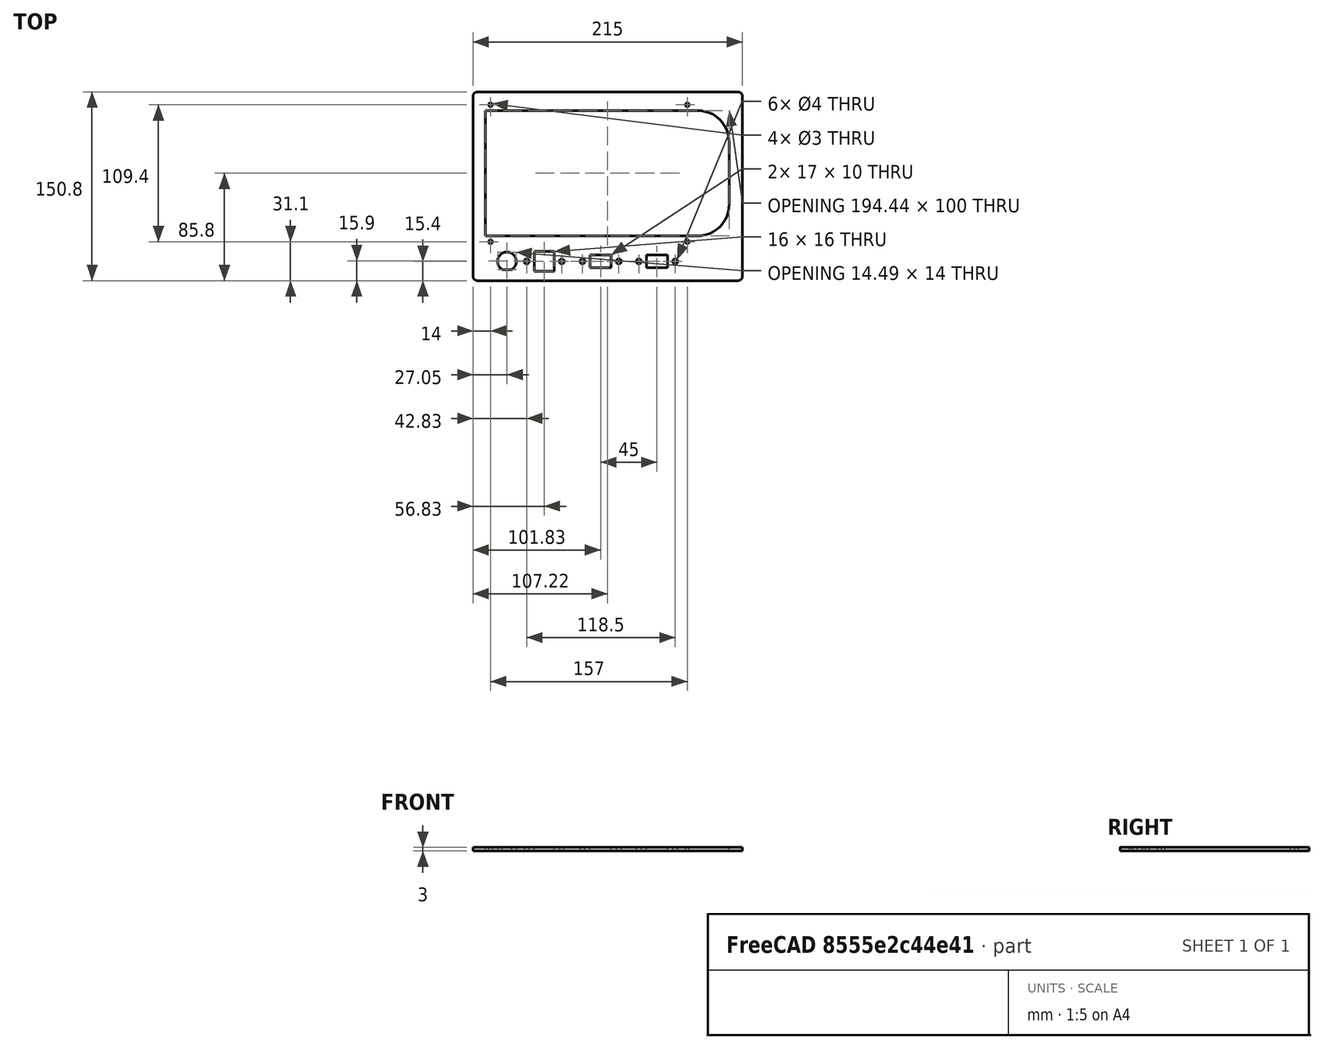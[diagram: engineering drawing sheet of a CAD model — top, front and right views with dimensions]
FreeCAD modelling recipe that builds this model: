
FCSTD DOCUMENT  (FreeCAD 0.20R29603 (Git))
Label: small
License: All rights reserved
LicenseURL: http://en.wikipedia.org/wiki/All_rights_reserved
objects: Sketcher::SketchObject×1, Part::Extrusion×1
note: 2 computed .brp shape members not serialized (recipe doc carries the construction recipe); baked Part::Feature solids carry a one-line shape summary decoded from their .brp

FEATURE [Sketcher::SketchObject] Sketch
  FullyConstrained = true
  sketch-geometry (74):
    g0: LineSegment StartX=-104 StartY=-75.4 StartZ=0 EndX=104 EndY=-75.4 EndZ=0
    g1: LineSegment StartX=107.5 StartY=-71.9 StartZ=0 EndX=107.5 EndY=71.9 EndZ=0
    g2: LineSegment StartX=104 StartY=75.4 StartZ=0 EndX=-104 EndY=75.4 EndZ=0
    g3: LineSegment StartX=-107.5 StartY=71.9 StartZ=0 EndX=-107.5 EndY=-71.9 EndZ=0
    g4: ArcOfCircle CenterX=-104 CenterY=71.9 CenterZ=0 NormalX=0 NormalY=0 NormalZ=1 AngleXU=0 Radius=3.5 StartAngle=1.5708 EndAngle=3.14159
    g5: ArcOfCircle CenterX=104 CenterY=71.9 CenterZ=0 NormalX=0 NormalY=0 NormalZ=1 AngleXU=0 Radius=3.5 StartAngle=-9e-16 EndAngle=1.5708
    g6: ArcOfCircle CenterX=104 CenterY=-71.9 CenterZ=0 NormalX=0 NormalY=0 NormalZ=1 AngleXU=0 Radius=3.5 StartAngle=4.71239 EndAngle=6.28319
    g7: ArcOfCircle CenterX=-104 CenterY=-71.9 CenterZ=0 NormalX=0 NormalY=0 NormalZ=1 AngleXU=0 Radius=3.5 StartAngle=3.14159 EndAngle=4.71239
    g8: LineSegment StartX=-97.5 StartY=-39.6 StartZ=0 EndX=67.5 EndY=-39.6 EndZ=0
    g9: LineSegment StartX=67.5 StartY=-39.6 StartZ=0 EndX=67.5 EndY=60.4 EndZ=0
    g10: LineSegment StartX=67.5 StartY=60.4 StartZ=0 EndX=-97.5 EndY=60.4 EndZ=0
    g11: LineSegment StartX=-97.5 StartY=60.4 StartZ=0 EndX=-97.5 EndY=-39.6 EndZ=0
    g12: Circle CenterX=-93.5 CenterY=65.1 CenterZ=0 NormalX=0 NormalY=0 NormalZ=1 AngleXU=0 Radius=1.5
    g13: Circle CenterX=63.5 CenterY=65.1 CenterZ=0 NormalX=0 NormalY=0 NormalZ=1 AngleXU=0 Radius=1.5
    g14: Circle CenterX=-93.5 CenterY=-44.3 CenterZ=0 NormalX=0 NormalY=0 NormalZ=1 AngleXU=0 Radius=1.5
    g15: Circle CenterX=63.5 CenterY=-44.3 CenterZ=0 NormalX=0 NormalY=0 NormalZ=1 AngleXU=0 Radius=1.5
    g16: LineSegment StartX=-97.5 StartY=60.4 StartZ=0 EndX=67.5 EndY=-39.6 EndZ=0
    g17: LineSegment StartX=-97.5 StartY=-39.6 StartZ=0 EndX=67.5 EndY=60.4 EndZ=0
    g18: GeomPoint X=-15 Y=10.4 Z=0
    g19: GeomPoint X=-15 Y=10.4 Z=0
    g20: LineSegment StartX=-15 StartY=65.1 StartZ=0 EndX=-15 EndY=10.4 EndZ=0
    g21: LineSegment StartX=-15 StartY=10.4 StartZ=0 EndX=-15 EndY=-44.3 EndZ=0
    g22: LineSegment StartX=-93.5 StartY=65.1 StartZ=0 EndX=63.5 EndY=65.1 EndZ=0
    g23: LineSegment StartX=-93.5 StartY=-44.3 StartZ=0 EndX=63.5 EndY=-44.3 EndZ=0
    g24: LineSegment StartX=-93.5 StartY=65.1 StartZ=0 EndX=-93.5 EndY=-44.3 EndZ=0
    g25: LineSegment StartX=67.5 StartY=60.4 StartZ=0 EndX=71.94 EndY=60.4 EndZ=0
    g26: LineSegment StartX=96.94 StartY=35.4 StartZ=0 EndX=96.94 EndY=-14.6 EndZ=0
    g27: LineSegment StartX=67.5 StartY=-39.6 StartZ=0 EndX=71.94 EndY=-39.6 EndZ=0
    g28: ArcOfCircle CenterX=71.94 CenterY=35.4 CenterZ=0 NormalX=0 NormalY=0 NormalZ=1 AngleXU=0 Radius=25 StartAngle=0 EndAngle=1.5708
    g29: ArcOfCircle CenterX=71.94 CenterY=-14.6 CenterZ=0 NormalX=0 NormalY=0 NormalZ=1 AngleXU=0 Radius=25 StartAngle=4.71239 EndAngle=6.28319
    g30: GeomPoint X=-93.5 Y=66.6 Z=0
    g31: GeomPoint X=-93.5 Y=-45.8 Z=0
    g32: ArcOfCircle CenterX=-80.45 CenterY=-60 CenterZ=0 NormalX=0 NormalY=0 NormalZ=1 AngleXU=0 Radius=7.5 StartAngle=5.2347 EndAngle=10.4733
    g33: LineSegment StartX=-84.1917 StartY=-66.5 StartZ=0 EndX=-76.7083 EndY=-66.5 EndZ=0
    g34: GeomPoint X=-80.45 Y=-52.5 Z=0
    g35: LineSegment StartX=-80.45 StartY=-52.5 StartZ=0 EndX=-80.45 EndY=-60 EndZ=0
    g36: LineSegment StartX=-14.17 StartY=-55 StartZ=0 EndX=2.83 EndY=-55 EndZ=0
    g37: LineSegment StartX=2.83 StartY=-55 StartZ=0 EndX=2.83 EndY=-65 EndZ=0
    g38: LineSegment StartX=2.83 StartY=-65 StartZ=0 EndX=-14.17 EndY=-65 EndZ=0
    g39: LineSegment StartX=-14.17 StartY=-65 StartZ=0 EndX=-14.17 EndY=-55 EndZ=0
    g40: LineSegment StartX=-14.17 StartY=-55 StartZ=0 EndX=2.83 EndY=-65 EndZ=0
    g41: LineSegment StartX=-14.17 StartY=-65 StartZ=0 EndX=2.83 EndY=-55 EndZ=0
    g42: GeomPoint X=-5.67 Y=-60 Z=0
    g43: Circle CenterX=-20.17 CenterY=-60 CenterZ=0 NormalX=0 NormalY=0 NormalZ=1 AngleXU=0 Radius=2
    g44: Circle CenterX=8.83 CenterY=-60 CenterZ=0 NormalX=0 NormalY=0 NormalZ=1 AngleXU=0 Radius=2
    g45: LineSegment StartX=-20.17 StartY=-60 StartZ=0 EndX=-5.67 EndY=-60 EndZ=0
    g46: LineSegment StartX=-5.67 StartY=-60 StartZ=0 EndX=8.83 EndY=-60 EndZ=0
    g47: GeomPoint X=-18.17 Y=-60 Z=0
    g48: GeomPoint X=6.83 Y=-60 Z=0
    g49: LineSegment StartX=-58.67 StartY=-68 StartZ=0 EndX=-42.67 EndY=-68 EndZ=0
    g50: LineSegment StartX=-42.67 StartY=-68 StartZ=0 EndX=-42.67 EndY=-52 EndZ=0
    g51: LineSegment StartX=-42.67 StartY=-52 StartZ=0 EndX=-58.67 EndY=-52 EndZ=0
    g52: LineSegment StartX=-58.67 StartY=-52 StartZ=0 EndX=-58.67 EndY=-68 EndZ=0
    g53: Circle CenterX=-64.67 CenterY=-60 CenterZ=0 NormalX=0 NormalY=0 NormalZ=1 AngleXU=0 Radius=2
    g54: Circle CenterX=-36.67 CenterY=-60 CenterZ=0 NormalX=0 NormalY=0 NormalZ=1 AngleXU=0 Radius=2
    g55: LineSegment StartX=-58.67 StartY=-52 StartZ=0 EndX=-42.67 EndY=-68 EndZ=0
    g56: LineSegment StartX=-58.67 StartY=-68 StartZ=0 EndX=-42.67 EndY=-52 EndZ=0
    g57: GeomPoint X=-50.67 Y=-60 Z=0
    g58: LineSegment StartX=-64.67 StartY=-60 StartZ=0 EndX=-50.67 EndY=-60 EndZ=0
    g59: LineSegment StartX=-36.67 StartY=-60 StartZ=0 EndX=-50.67 EndY=-60 EndZ=0
    g60: LineSegment StartX=-80.45 StartY=-60 StartZ=0 EndX=-50.67 EndY=-60 EndZ=0
    g61: LineSegment StartX=-50.67 StartY=-60 StartZ=0 EndX=-5.67 EndY=-60 EndZ=0
    g62: LineSegment StartX=30.83 StartY=-65 StartZ=0 EndX=47.83 EndY=-65 EndZ=0
    g63: LineSegment StartX=47.83 StartY=-65 StartZ=0 EndX=47.83 EndY=-55 EndZ=0
    g64: LineSegment StartX=47.83 StartY=-55 StartZ=0 EndX=30.83 EndY=-55 EndZ=0
    g65: LineSegment StartX=30.83 StartY=-55 StartZ=0 EndX=30.83 EndY=-65 EndZ=0
    g66: Circle CenterX=24.83 CenterY=-60 CenterZ=0 NormalX=0 NormalY=0 NormalZ=1 AngleXU=0 Radius=2
    g67: Circle CenterX=53.83 CenterY=-60 CenterZ=0 NormalX=0 NormalY=0 NormalZ=1 AngleXU=0 Radius=2
    g68: LineSegment StartX=30.83 StartY=-55 StartZ=0 EndX=47.83 EndY=-65 EndZ=0
    g69: LineSegment StartX=30.83 StartY=-65 StartZ=0 EndX=47.83 EndY=-55 EndZ=0
    g70: GeomPoint X=39.33 Y=-60 Z=0
    g71: LineSegment StartX=24.83 StartY=-60 StartZ=0 EndX=39.33 EndY=-60 EndZ=0
    g72: LineSegment StartX=39.33 StartY=-60 StartZ=0 EndX=53.83 EndY=-60 EndZ=0
    g73: LineSegment StartX=-5.67 StartY=-60 StartZ=0 EndX=39.33 EndY=-60 EndZ=0
  constraints (181):
    c: Horizontal(g0)
    c: Horizontal(g2)
    c: Vertical(g1)
    c: Vertical(g3)
    c: Tangent(g2,g4) = -1.5708
    c: Tangent(g3,g4) = -1.5708
    c: Tangent(g1,g5) = -1.5708
    c: Tangent(g2,g5) = -1.5708
    c: Tangent(g0,g6) = -1.5708
    c: Tangent(g1,g6) = -1.5708
    c: Tangent(g0,g7) = -1.5708
    c: Tangent(g3,g7) = -1.5708
    c: Equal(g4,g5)
    c: Equal(g5,g6)
    c: Equal(g7,g6)
    c: DistanceX(g3,g4) = 3.5
    c: Coincident(g8,g9)
    c: Coincident(g9,g10)
    c: Coincident(g10,g11)
    c: Coincident(g11,g8)
    c: Horizontal(g8)
    c: Horizontal(g10)
    c: Vertical(g9)
    c: Vertical(g11)
    c: Equal(g12,g13)
    c: Equal(g13,g15)
    c: Equal(g15,g14)
    c: Coincident(g16,g10)
    c: Coincident(g16,g8)
    c: Coincident(g17,g8)
    c: Coincident(g17,g9)
    c: PointOnObject(g18,g16)
    c: PointOnObject(g19,g17)
    c: Coincident(g18,g19)
    c: Coincident(g20,g18)
    c: Coincident(g21,g18)
    c: Vertical(g20)
    c: Vertical(g21)
    c: Equal(g20,g21)
    c: Symmetric(g12,g13,g20)
    c: Symmetric(g14,g15,g21)
    c: Coincident(g22,g12)
    c: Coincident(g22,g13)
    c: Horizontal(g22)
    c: Coincident(g23,g14)
    c: Coincident(g23,g15)
    c: Horizontal(g23)
    c: Coincident(g24,g12)
    c: Coincident(g24,g14)
    c: Vertical(g24)
    c: DistanceX(g10,g12) = 4
    c: DistanceX(g8,g8) = 165
    c: DistanceY(g9,g9) = 100
    c: Coincident(g25,g9)
    c: Vertical(g26)
    c: Coincident(g27,g8)
    c: Horizontal(g25)
    c: Horizontal(g27)
    c: Tangent(g25,g28) = 1.5708
    c: Tangent(g26,g28) = 1.5708
    c: Tangent(g26,g29) = 1.5708
    c: Tangent(g27,g29) = -1.5708
    c: Equal(g28,g29)
    c: DistanceX(g25,g25) = 4.44
    c: DistanceX(g3,g10) = 10
    c: DistanceY(g10,g2) = 15
    c: Diameter(g14) = 3
    c: Radius(g28) = 25
    c: PointOnObject(g30,g12)
    c: PointOnObject(g30,g24)
    c: PointOnObject(g31,g14)
    c: PointOnObject(g31,g24)
    c: DistanceY(g31,g30) = 112.4
    c: DistanceX(g3,g1) = 215
    c: DistanceY(g0,g2) = 150.8
    c: Symmetric(g4,g6,g-1)
    c: Coincident(g33,g32)
    c: Coincident(g33,g32)
    c: Horizontal(g33)
    c: PointOnObject(g34,g32)
    c: Coincident(g35,g34)
    c: Coincident(g35,g32)
    c: Vertical(g35)
    c: DistanceY(g32,g34) = 14
    c: DistanceY(g35,g35) = 7.5
    c: DistanceY(g7,g32) = 11.9
    c: DistanceX(g7,g32) = 23.55
    c: Coincident(g36,g37)
    c: Coincident(g37,g38)
    c: Coincident(g38,g39)
    c: Coincident(g39,g36)
    c: Horizontal(g36)
    c: Horizontal(g38)
    c: Vertical(g37)
    c: Vertical(g39)
    c: DistanceX(g36,g36) = 17
    c: DistanceY(g39,g39) = 10
    c: Coincident(g40,g36)
    c: Coincident(g40,g37)
    c: Coincident(g41,g38)
    c: Coincident(g41,g36)
    c: PointOnObject(g42,g40)
    c: PointOnObject(g42,g41)
    c: Equal(g44,g43)
    c: Coincident(g45,g43)
    c: Coincident(g45,g42)
    c: Horizontal(g45)
    c: Coincident(g46,g42)
    c: Coincident(g46,g44)
    c: Horizontal(g46)
    c: Equal(g45,g46)
    c: PointOnObject(g47,g43)
    c: PointOnObject(g48,g44)
    c: PointOnObject(g48,g46)
    c: PointOnObject(g47,g45)
    c: DistanceX(g47,g48) = 25
    c: Diameter(g44) = 4
    c: Coincident(g49,g50)
    c: Coincident(g50,g51)
    c: Coincident(g51,g52)
    c: Coincident(g52,g49)
    c: Horizontal(g49)
    c: Horizontal(g51)
    c: Vertical(g50)
    c: Vertical(g52)
    c: DistanceX(g51,g51) = 16
    c: DistanceY(g50,g50) = 16
    c: Equal(g54,g53)
    c: Equal(g54,g43)
    c: Coincident(g55,g51)
    c: Coincident(g55,g49)
    c: Coincident(g56,g49)
    c: Coincident(g56,g50)
    c: PointOnObject(g57,g55)
    c: PointOnObject(g57,g56)
    c: Coincident(g58,g53)
    c: Coincident(g58,g57)
    c: Coincident(g59,g54)
    c: Coincident(g59,g57)
    c: Equal(g58,g59)
    c: Horizontal(g59)
    c: Horizontal(g58)
    c: DistanceX(g53,g54) = 28
    c: Coincident(g60,g32)
    c: Coincident(g60,g57)
    c: Horizontal(g60)
    c: DistanceX(g32,g57) = 29.78
    c: DistanceX(g57,g42) = 45
    c: Coincident(g61,g57)
    c: Coincident(g61,g42)
    c: Horizontal(g61)
    c: Coincident(g62,g63)
    c: Coincident(g63,g64)
    c: Coincident(g64,g65)
    c: Coincident(g65,g62)
    c: Horizontal(g62)
    c: Horizontal(g64)
    c: Vertical(g63)
    c: Vertical(g65)
    c: Equal(g64,g36)
    c: Equal(g37,g65)
    c: Equal(g67,g66)
    c: Equal(g66,g44)
    c: Coincident(g68,g64)
    c: Coincident(g68,g62)
    c: Coincident(g69,g62)
    c: Coincident(g69,g63)
    c: PointOnObject(g70,g69)
    c: PointOnObject(g70,g68)
    c: Coincident(g71,g66)
    c: Coincident(g71,g70)
    c: Coincident(g72,g67)
    c: Horizontal(g72)
    c: Horizontal(g71)
    c: Equal(g71,g72)
    c: Equal(g46,g71)
    c: Coincident(g72,g70)
    c: Coincident(g73,g42)
    c: Coincident(g73,g70)
    c: Horizontal(g73)
    c: DistanceX(g42,g70) = 45
FEATURE [Part::Extrusion] Extrude
  Base = -> Sketch
  Dir = (0,0,1)
  DirMode = 2
  FaceMakerClass = Part::FaceMakerBullseye
  LengthFwd = 3
  LengthRev = 0
  Solid = true
  Symmetric = false
